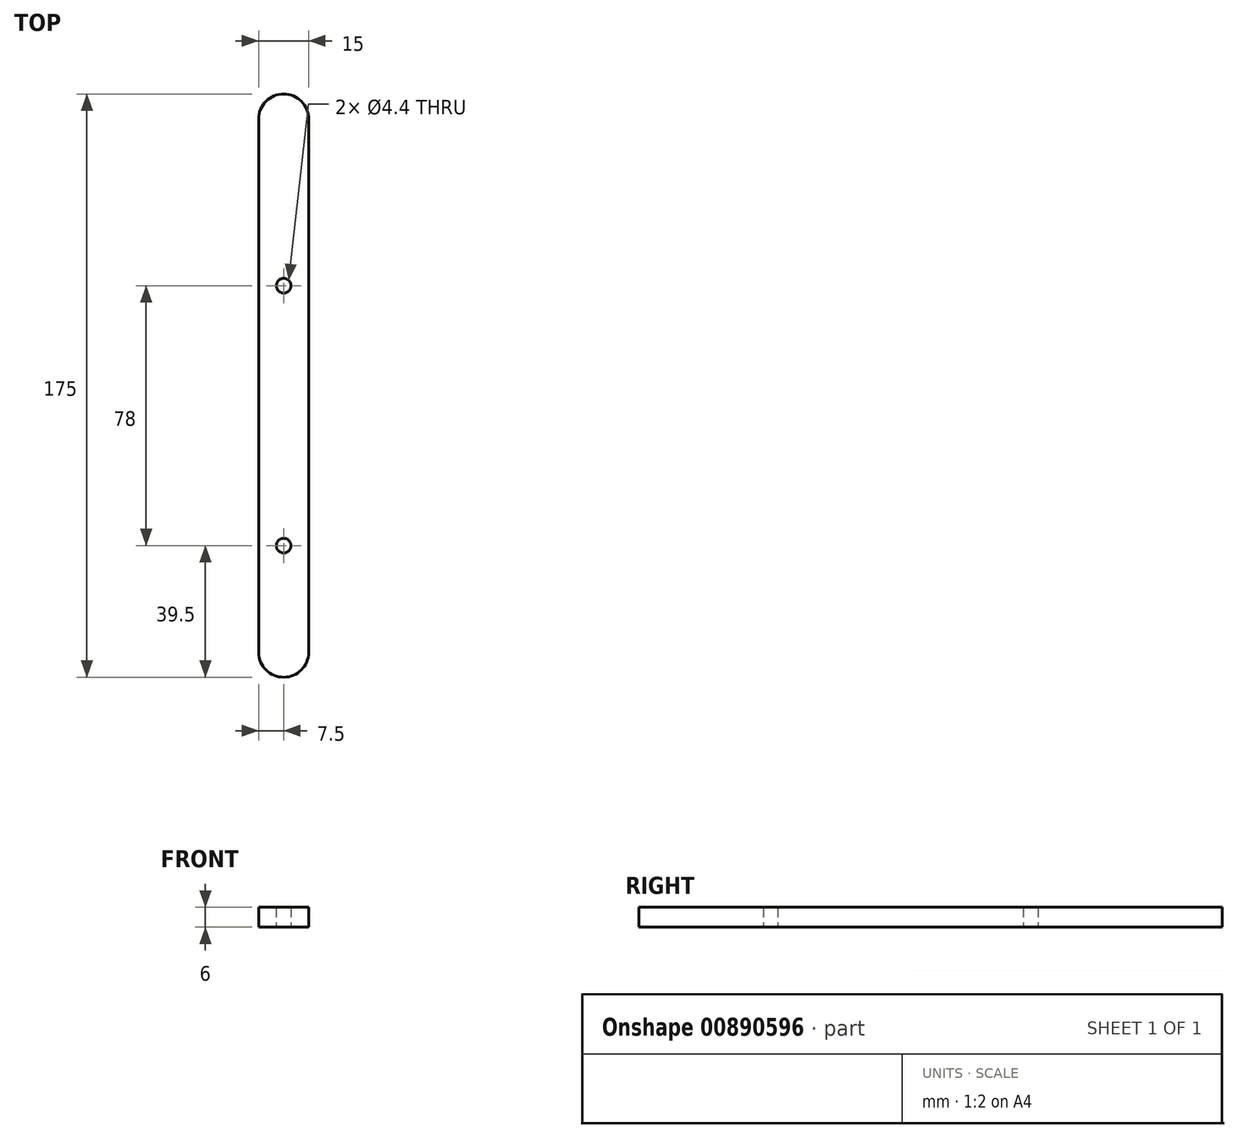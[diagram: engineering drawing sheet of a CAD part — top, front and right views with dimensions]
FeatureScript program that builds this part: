
annotation { "Feature Type Name" : "Feature", "Feature Type Description" : "" }
export const myFeature = defineFeature(function(context is Context, id is Id, definition is map)
    precondition{}
    {
        {
            var Q0;
            Q0=qCreatedBy(makeId("Top.planeOp"),FACE);
            var sketch = newSketch(context, id + "F0", { "sketchPlane" : qUnion([Q0])});
            skLineSegment(sketch, "E0.bottom", {"start": v(7.5, 80) * mm, "end": v(-7.5, 80) * mm});
            skLineSegment(sketch, "E0.top", {"start": v(7.5, -80) * mm, "end": v(-7.5, -80) * mm});
            skLineSegment(sketch, "E0.left", {"start": v(7.5, 80) * mm, "end": v(7.5, -80) * mm});
            skLineSegment(sketch, "E0.right", {"start": v(-7.5, 80) * mm, "end": v(-7.5, -80) * mm});
            skPoint(sketch, "E0.middle", {"position": v(0, 0) * mm});
            skLineSegment(sketch, "E1", {"start": v(0, 80) * mm, "end": v(0, -80) * mm, "construction": true});
            skCircle(sketch, "E2", {"center": v(0, -48) * mm, "radius": 2.2 * mm});
            skCircle(sketch, "E3", {"center": v(0, 30) * mm, "radius": 2.2 * mm});
            skArc(sketch, "E4", {"start": v(7.5, 80) * mm, "mid": v(0, 87.5) * mm, "end": v(-7.5, 80) * mm});
            skArc(sketch, "E5", {"start": v(-7.5, -80) * mm, "mid": v(0, -87.5) * mm, "end": v(7.5, -80) * mm});
            skSolve(sketch);
        }
        {
            var Q0;
            Q0=makeQuery(id+"F0.imprint","IMPRINT",FACE,{"disambiguationData":[TD([[makeQuery(id+"F0.imprint","IMPRINT",EDGE,{"derivedFrom":sQuery(id+"F0.wireOp",EDGE,"E0.bottom")}),1.0]])]});
            var Q1;
            Q1=makeQuery(id+"F0.imprint","IMPRINT",FACE,{"disambiguationData":[TD([[makeQuery(id+"F0.imprint","IMPRINT",EDGE,{"derivedFrom":sQuery(id+"F0.wireOp",EDGE,"E0.bottom")}),-1.0]])]});
            var Q2;
            Q2=makeQuery(id+"F0.imprint","IMPRINT",FACE,{"disambiguationData":[TD([[makeQuery(id+"F0.imprint","IMPRINT",EDGE,{"derivedFrom":sQuery(id+"F0.wireOp",EDGE,"E0.top")}),1.0]])]});
            extrude(context, id + "F1", {"entities" : qUnion([Q0, Q1, Q2]), "depth" : 6 * mm, "offsetDistance" : 25 * mm});
        }
    });
